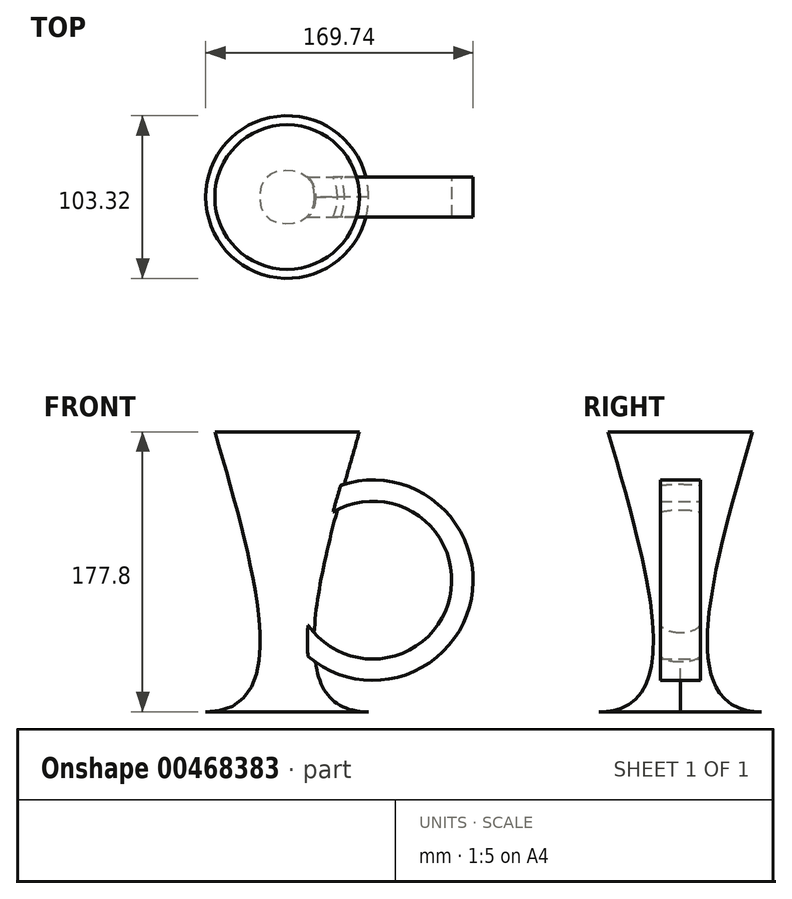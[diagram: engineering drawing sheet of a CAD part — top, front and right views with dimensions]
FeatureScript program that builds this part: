
annotation { "Feature Type Name" : "Feature", "Feature Type Description" : "" }
export const myFeature = defineFeature(function(context is Context, id is Id, definition is map)
    precondition{}
    {
        {
            var Q0;
            Q0=qCreatedBy(makeId("Top.planeOp"),FACE);
            var sketch = newSketch(context, id + "F0", { "sketchPlane" : qUnion([Q0])});
            skCircle(sketch, "E0", {"center": v(0, 0) * mm, "radius": 51.66 * mm});
            skSolve(sketch);
        }
        {
            var Q0;
            Q0=qCreatedBy(makeId("Top.planeOp"),FACE);
            cPlane(context, id + "F1", {"entities" : qUnion([Q0]), "cplaneType" : CPlaneType.OFFSET, "offset" : 177.8 * mm, "width" : 152.4 * mm, "height" : 152.4 * mm});
        }
        {
            var Q0;
            Q0=qCreatedBy(id+"F1.planeOp",FACE);
            var sketch = newSketch(context, id + "F2", { "sketchPlane" : qUnion([Q0])});
            skCircle(sketch, "E1", {"center": v(0, 0) * mm, "radius": 45.91 * mm});
            skSolve(sketch);
        }
        {
            var Q0;
            Q0=makeQuery(id+"F0.imprint","IMPRINT",FACE,{"disambiguationData":[TD([[makeQuery(id+"F0.imprint","IMPRINT",EDGE,{"derivedFrom":sQuery(id+"F0.wireOp",EDGE,"E0")}),1.0]])]});
            var Q1;
            Q1=makeQuery(id+"F2.imprint","IMPRINT",FACE,{"disambiguationData":[TD([[makeQuery(id+"F2.imprint","IMPRINT",EDGE,{"derivedFrom":sQuery(id+"F2.wireOp",EDGE,"E1")}),1.0]])]});
            loft(context, id + "F3", {"startCondition" : LoftEndDerivativeType.TANGENT_TO_PROFILE, "startMagnitude" : 30, "sheetProfilesArray" : [{ "sheetProfileEntities" : qUnion([Q0]) }, { "sheetProfileEntities" : qUnion([Q1]) }]});
        }
        {
            var Q0;
            Q0=qCreatedBy(makeId("Front.planeOp"),FACE);
            var sketch = newSketch(context, id + "F4", { "sketchPlane" : qUnion([Q0])});
            skCircle(sketch, "E2", {"center": v(54.47, 83.6) * mm, "radius": 63.6 * mm});
            skCircle(sketch, "E3", {"center": v(54.47, 83.6) * mm, "radius": 50.1 * mm});
            skSolve(sketch);
        }
        {
            var Q0;
            Q0 = qSketchRegion(id + "F4", true);
            extrude(context, id + "F5", {"entities" : qUnion([Q0]), "operationType" : NewBodyOperationType.ADD, "endBound" : BoundingType.SYMMETRIC, "depth" : 25.4 * mm});
        }
    });
